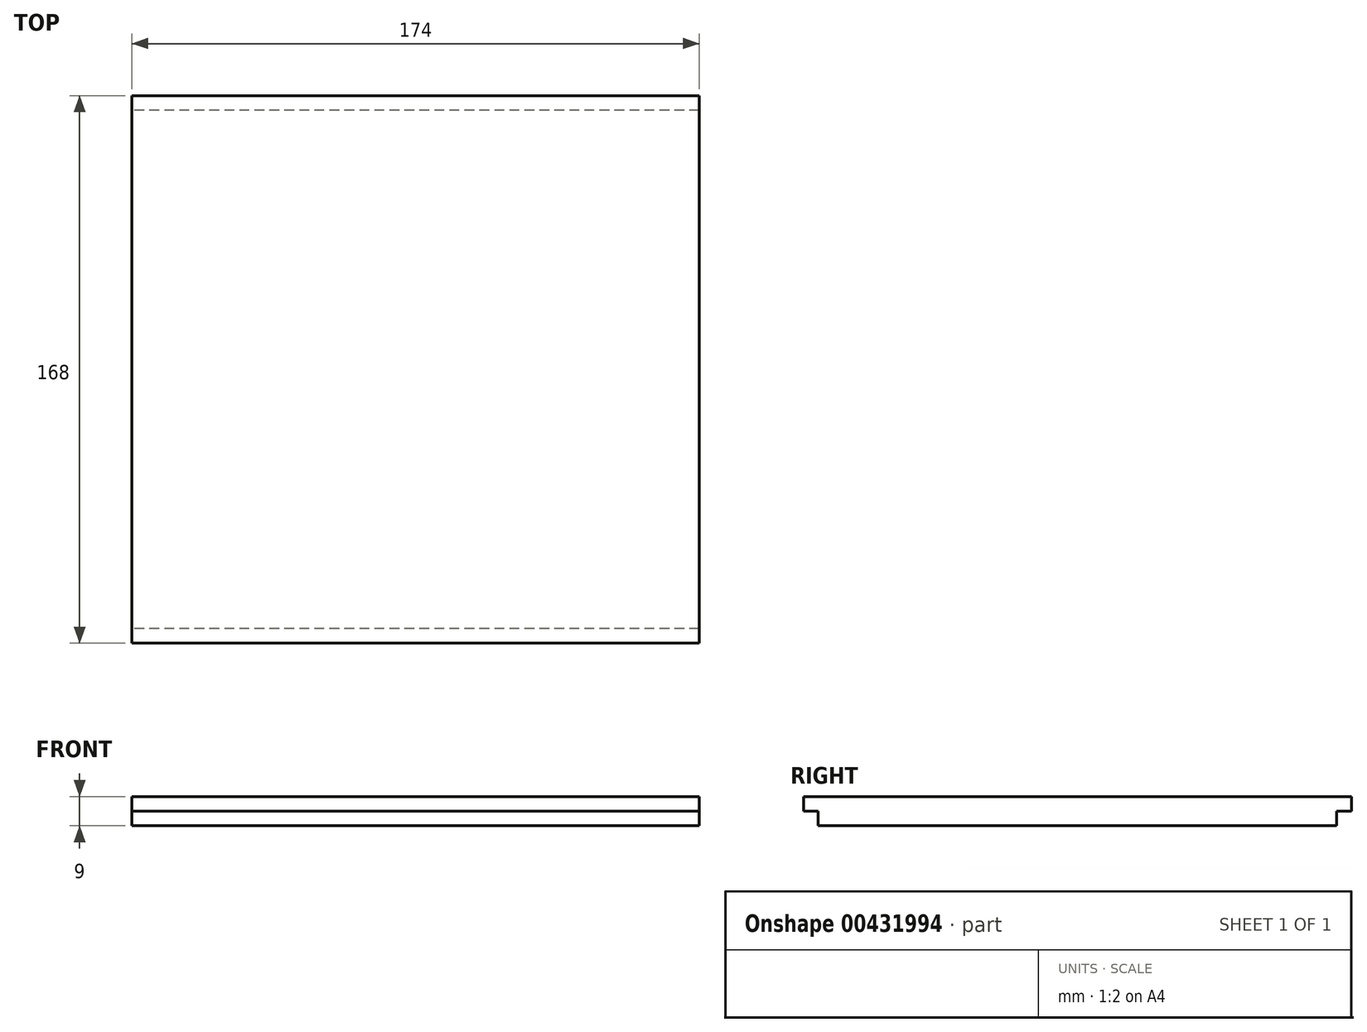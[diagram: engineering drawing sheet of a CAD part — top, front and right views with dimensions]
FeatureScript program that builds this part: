
annotation { "Feature Type Name" : "Feature", "Feature Type Description" : "" }
export const myFeature = defineFeature(function(context is Context, id is Id, definition is map)
    precondition{}
    {
        {
            var Q0;
            Q0=qCreatedBy(makeId("Top.planeOp"),FACE);
            var sketch = newSketch(context, id + "F0", { "sketchPlane" : qUnion([Q0])});
            skLineSegment(sketch, "E0.bottom", {"start": v(-87, 84) * mm, "end": v(87, 84) * mm});
            skLineSegment(sketch, "E0.top", {"start": v(-87, -84) * mm, "end": v(87, -84) * mm});
            skLineSegment(sketch, "E0.left", {"start": v(-87, 84) * mm, "end": v(-87, -84) * mm});
            skLineSegment(sketch, "E0.right", {"start": v(87, 84) * mm, "end": v(87, -84) * mm});
            skPoint(sketch, "E0.middle", {"position": v(0, 0) * mm});
            skSolve(sketch);
        }
        {
            var Q0;
            Q0=qSketchRegion(id+"F0",true);
            extrude(context, id + "F1", {"entities" : qUnion([Q0]), "depth" : 9 * mm, "offsetDistance" : 25 * mm});
        }
        {
            var Q0;
            Q0=makeQuery(id+"F1.opExtrude","CAP_FACE",FACE,{"disambiguationData":[OSD([sQuery(id+"F0.wireOp",EDGE,"E0.bottom"),sQuery(id+"F0.wireOp",EDGE,"E0.top"),sQuery(id+"F0.wireOp",EDGE,"E0.left"),sQuery(id+"F0.wireOp",EDGE,"E0.right")])],"isStart":true});
            var sketch = newSketch(context, id + "F2", { "sketchPlane" : qUnion([Q0])});
            skLineSegment(sketch, "E1.bottom", {"start": v(87, 84) * mm, "end": v(-87, 84) * mm});
            skLineSegment(sketch, "E1.top", {"start": v(87, 79.5) * mm, "end": v(-87, 79.5) * mm});
            skLineSegment(sketch, "E1.left", {"start": v(87, 84) * mm, "end": v(87, 79.5) * mm});
            skLineSegment(sketch, "E1.right", {"start": v(-87, 84) * mm, "end": v(-87, 79.5) * mm});
            skLineSegment(sketch, "E2.bottom", {"start": v(87, -84) * mm, "end": v(-87, -84) * mm});
            skLineSegment(sketch, "E2.top", {"start": v(87, -79.5) * mm, "end": v(-87, -79.5) * mm});
            skLineSegment(sketch, "E2.left", {"start": v(87, -84) * mm, "end": v(87, -79.5) * mm});
            skLineSegment(sketch, "E2.right", {"start": v(-87, -84) * mm, "end": v(-87, -79.5) * mm});
            skSolve(sketch);
        }
        {
            var Q0;
            Q0=qSketchRegion(id+"F2",true);
            extrude(context, id + "F3", {"entities" : qUnion([Q0]), "operationType" : NewBodyOperationType.REMOVE, "oppositeDirection" : true, "depth" : 4.5 * mm, "offsetDistance" : 25 * mm});
        }
    });
